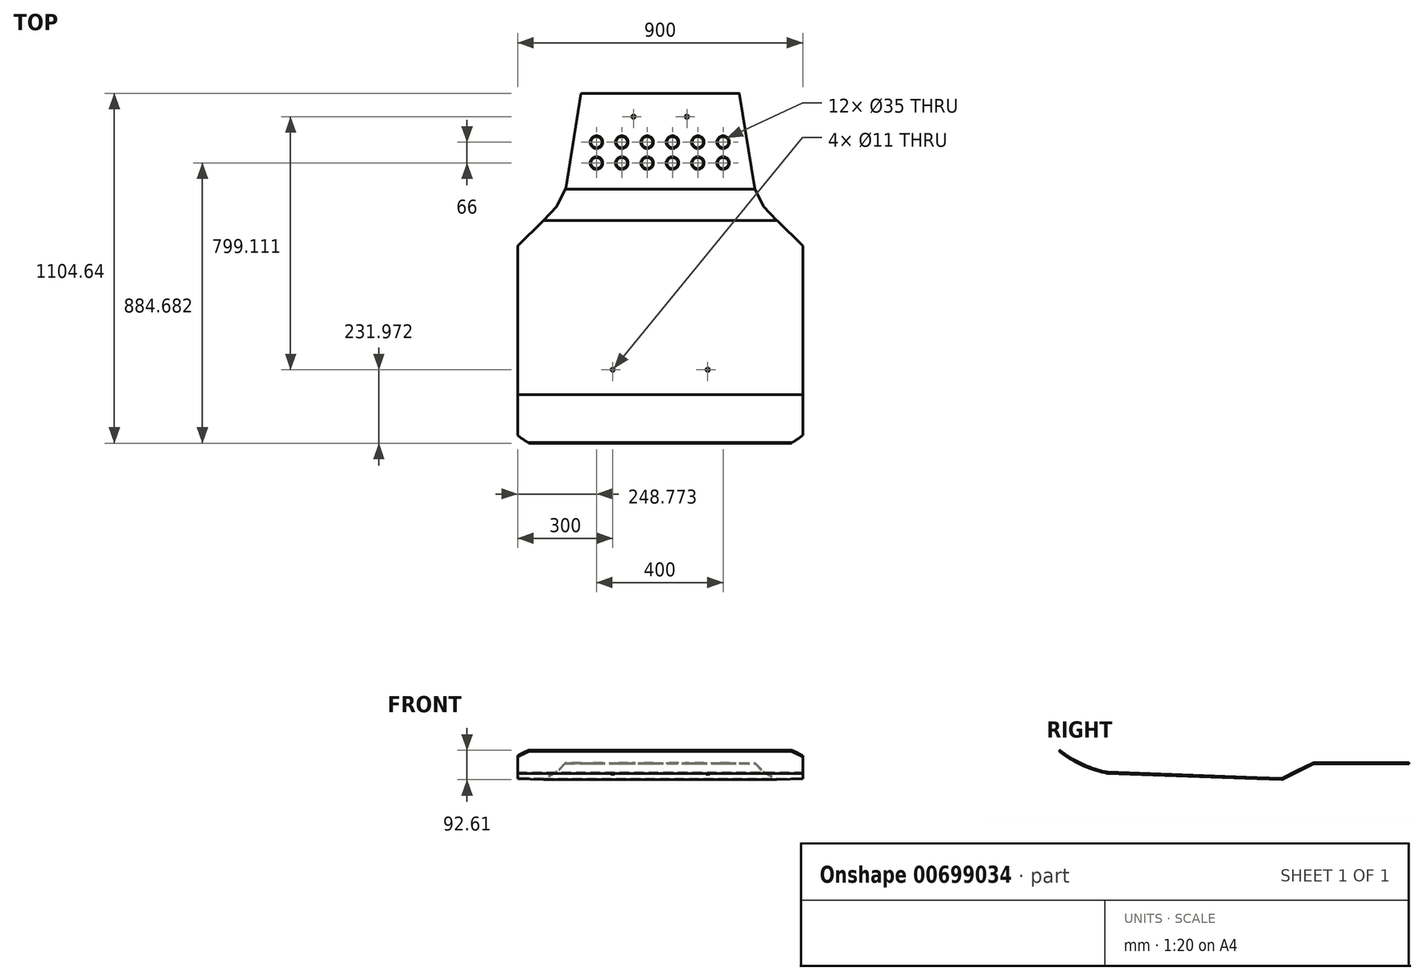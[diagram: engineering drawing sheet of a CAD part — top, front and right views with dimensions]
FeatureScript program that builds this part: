
annotation { "Feature Type Name" : "Feature", "Feature Type Description" : "" }
export const myFeature = defineFeature(function(context is Context, id is Id, definition is map)
    precondition{}
    {
        {
            var Q0;
            Q0=qCreatedBy(makeId("Right.planeOp"),FACE);
            cPlane(context, id + "F0", {"entities" : qUnion([Q0]), "cplaneType" : CPlaneType.OFFSET, "offset" : 450 * mm, "width" : 150 * mm, "height" : 150 * mm});
        }
        {
            var Q0;
            Q0=qCreatedBy(id+"F0.planeOp",FACE);
            var sketch = newSketch(context, id + "F1", { "sketchPlane" : qUnion([Q0])});
            skLineSegment(sketch, "E0", {"start": v(633.45, 19.14) * mm, "end": v(333.45, 19.14) * mm});
            skLineSegment(sketch, "E1", {"start": v(333.45, 19.14) * mm, "end": v(233.45, -30.86) * mm});
            skLineSegment(sketch, "E2", {"start": v(233.45, -30.86) * mm, "end": v(-316.55, -10.86) * mm});
            skArc(sketch, "E3", {"start": v(-316.55, -10.86) * mm, "mid": v(-395.73, 14.26) * mm, "end": v(-466.55, 57.68) * mm});
            skArc(sketch, "E4.0", {"start": v(-316.99, -14.85) * mm, "mid": v(-397.25, 10.56) * mm, "end": v(-469.03, 54.55) * mm});
            skLineSegment(sketch, "E4.1", {"start": v(234.33, -34.9) * mm, "end": v(-316.99, -14.85) * mm});
            skLineSegment(sketch, "E4.2", {"start": v(334.4, 15.14) * mm, "end": v(234.33, -34.9) * mm});
            skLineSegment(sketch, "E4.3", {"start": v(633.45, 15.14) * mm, "end": v(334.4, 15.14) * mm});
            skArc(sketch, "E5", {"start": v(-466.55, 57.68) * mm, "mid": v(-468.7, 56.83) * mm, "end": v(-469.03, 54.55) * mm});
            skArc(sketch, "E6", {"start": v(633.45, 15.14) * mm, "mid": v(635.45, 17.14) * mm, "end": v(633.45, 19.14) * mm});
            skSolve(sketch);
        }
        {
            var Q0;
            Q0=makeQuery(id+"F1.imprint","IMPRINT",FACE,{"disambiguationData":[TD([[makeQuery(id+"F1.imprint","IMPRINT",EDGE,{"derivedFrom":sQuery(id+"F1.wireOp",EDGE,"E0")}),1.0]])]});
            var Q1;
            Q1=qCreatedBy(makeId("Right.planeOp"),FACE);
            extrude(context, id + "F2", {"entities" : qUnion([Q0]), "endBound" : BoundingType.UP_TO_SURFACE, "oppositeDirection" : true, "depth" : 25 * mm, "endBoundEntityFace" : qUnion([Q1]), "offsetDistance" : 25 * mm});
        }
        {
            var Q0;
            Q0=qCreatedBy(makeId("Top.planeOp"),FACE);
            cPlane(context, id + "F3", {"entities" : qUnion([Q0]), "cplaneType" : CPlaneType.OFFSET, "offset" : 100 * mm, "width" : 150 * mm, "height" : 150 * mm});
        }
        {
            var Q0;
            Q0=qCreatedBy(id+"F3.planeOp",FACE);
            var sketch = newSketch(context, id + "F4", { "sketchPlane" : qUnion([Q0])});
            skLineSegment(sketch, "E7", {"start": v(218.78, 735.39) * mm, "end": v(237, 712.97) * mm});
            skLineSegment(sketch, "E8", {"start": v(237, 712.97) * mm, "end": v(297.96, 337.61) * mm});
            skLineSegment(sketch, "E9", {"start": v(326.32, 278.4) * mm, "end": v(368.65, 233.6) * mm});
            skLineSegment(sketch, "E10", {"start": v(368.65, 233.6) * mm, "end": v(451.1, 153.37) * mm});
            skLineSegment(sketch, "E11", {"start": v(451.1, 153.37) * mm, "end": v(483.61, 153.37) * mm});
            skLineSegment(sketch, "E12", {"start": v(483.61, 153.37) * mm, "end": v(498.52, 703.49) * mm});
            skLineSegment(sketch, "E13", {"start": v(498.52, 703.49) * mm, "end": v(218.78, 735.39) * mm});
            skLineSegment(sketch, "E14", {"start": v(297.96, 337.61) * mm, "end": v(326.32, 278.4) * mm});
            skSolve(sketch);
        }
        {
            var Q0;
            Q0=makeQuery(id+"F4.imprint","IMPRINT",FACE,{"disambiguationData":[TD([[makeQuery(id+"F4.imprint","IMPRINT",EDGE,{"derivedFrom":sQuery(id+"F4.wireOp",EDGE,"E7")}),1.0]])]});
            extrude(context, id + "F5", {"entities" : qUnion([Q0]), "operationType" : NewBodyOperationType.REMOVE, "oppositeDirection" : true, "depth" : 137 * mm, "offsetDistance" : 25 * mm});
        }
        {
            var Q0;
            Q0=qCreatedBy(id+"F3.planeOp",FACE);
            var sketch = newSketch(context, id + "F6", { "sketchPlane" : qUnion([Q0])});
            skArc(sketch, "E15", {"start": v(367.93, -489.56) * mm, "mid": v(427.88, -460.38) * mm, "end": v(478.84, -417.38) * mm});
            skLineSegment(sketch, "E16", {"start": v(478.84, -417.38) * mm, "end": v(478.84, -496.6) * mm});
            skLineSegment(sketch, "E17", {"start": v(478.84, -496.6) * mm, "end": v(367.93, -489.56) * mm});
            skSolve(sketch);
        }
        {
            var Q0;
            Q0=makeQuery(id+"F6.imprint","IMPRINT",FACE,{"disambiguationData":[TD([[makeQuery(id+"F6.imprint","IMPRINT",EDGE,{"derivedFrom":sQuery(id+"F6.wireOp",EDGE,"E15")}),-1.0]])]});
            extrude(context, id + "F7", {"entities" : qUnion([Q0]), "operationType" : NewBodyOperationType.REMOVE, "endBound" : BoundingType.THROUGH_ALL, "oppositeDirection" : true, "depth" : 100 * mm, "offsetDistance" : 25 * mm});
        }
        {
            var Q0;
            Q0=makeQuery(id+"F2.opExtrude","SWEPT_FACE",FACE,{"disambiguationData":[OSD([sQuery(id+"F1.wireOp",EDGE,"E0")])]});
            var sketch = newSketch(context, id + "F8", { "sketchPlane" : qUnion([Q0])});
            skCircle(sketch, "E18", {"center": v(84.24, 561.9) * mm, "radius": 13.36 * mm});
            skSolve(sketch);
        }
        {
            var Q0;
            Q0=sQuery(id+"F8.wireOp",VERTEX,"E18.center");
            var Q1;
            Q1=makeQuery(id+"F2.opExtrude","SWEPT_BODY",BODY,{"disambiguationData":[OSD([sQuery(id+"F1.wireOp",EDGE,"E0"),sQuery(id+"F1.wireOp",EDGE,"E1"),sQuery(id+"F1.wireOp",EDGE,"E2"),sQuery(id+"F1.wireOp",EDGE,"E3"),sQuery(id+"F1.wireOp",EDGE,"E4.0"),sQuery(id+"F1.wireOp",EDGE,"E4.1"),sQuery(id+"F1.wireOp",EDGE,"E4.2"),sQuery(id+"F1.wireOp",EDGE,"E4.3"),sQuery(id+"F1.wireOp",EDGE,"E5"),sQuery(id+"F1.wireOp",EDGE,"E6")])]});
            hole(context, id + "F9", {"style" : HoleStyle.SIMPLE, "endStyle" : HoleEndStyle.THROUGH, "standardTappedOrClearance" : lookupTablePath({ "standard" : "ISO", "fit" : "Normal", "size" : "M10", "type" : "Clearance" }), "standardBlindInLast" : lookupTablePath({ "fit" : "Standard", "standard" : "ISO", "size" : "M10", "type" : "Clearance" }), "holeDiameter" : 11 * mm, "majorDiameter" : 5 * mm, "isTappedThrough" : true, "tappedDepth" : 12 * mm, "tapClearance" : 3, "startFromSketch" : true, "locations" : qUnion([Q0]), "scope" : qUnion([Q1])});
        }
        {
            var Q0;
            Q0=makeQuery(id+"F2.opExtrude","SWEPT_BODY",BODY,{"disambiguationData":[OSD([sQuery(id+"F1.wireOp",EDGE,"E0"),sQuery(id+"F1.wireOp",EDGE,"E1"),sQuery(id+"F1.wireOp",EDGE,"E2"),sQuery(id+"F1.wireOp",EDGE,"E3"),sQuery(id+"F1.wireOp",EDGE,"E4.0"),sQuery(id+"F1.wireOp",EDGE,"E4.1"),sQuery(id+"F1.wireOp",EDGE,"E4.2"),sQuery(id+"F1.wireOp",EDGE,"E4.3"),sQuery(id+"F1.wireOp",EDGE,"E5"),sQuery(id+"F1.wireOp",EDGE,"E6")])]});
            var Q1;
            Q1=qCreatedBy(makeId("Right.planeOp"),FACE);
            mirror(context, id + "F10", {"operationType" : NewBodyOperationType.ADD, "entities" : qUnion([Q0]), "mirrorPlane" : qUnion([Q1])});
        }
        {
            var Q0;
            {var subQ0=makeQuery(id+"F2.opExtrude","SWEPT_FACE",FACE,{"disambiguationData":[OSD([sQuery(id+"F1.wireOp",EDGE,"E2")])]});Q0=makeQuery(id+"F10.boolean.opBoolean","MERGE",FACE,{"derivedFrom":[subQ0,makeQuery(id+"F10.opPattern","COPY",FACE,{"derivedFrom":subQ0,"instanceName":"1"})]});}
            var sketch = newSketch(context, id + "F11", { "sketchPlane" : qUnion([Q0])});
            skCircle(sketch, "E19", {"center": v(150, -236.43) * mm, "radius": 5 * mm});
            skCircle(sketch, "E20", {"center": v(-150, -236.43) * mm, "radius": 5 * mm});
            skSolve(sketch);
        }
        {
            var Q0;
            Q0=sQuery(id+"F11.wireOp",VERTEX,"E20.center");
            var Q1;
            Q1=sQuery(id+"F11.wireOp",VERTEX,"E19.center");
            var Q2;
            Q2=makeQuery(id+"F2.opExtrude","SWEPT_BODY",BODY,{"disambiguationData":[OSD([sQuery(id+"F1.wireOp",EDGE,"E0"),sQuery(id+"F1.wireOp",EDGE,"E1"),sQuery(id+"F1.wireOp",EDGE,"E2"),sQuery(id+"F1.wireOp",EDGE,"E3"),sQuery(id+"F1.wireOp",EDGE,"E4.0"),sQuery(id+"F1.wireOp",EDGE,"E4.1"),sQuery(id+"F1.wireOp",EDGE,"E4.2"),sQuery(id+"F1.wireOp",EDGE,"E4.3"),sQuery(id+"F1.wireOp",EDGE,"E5"),sQuery(id+"F1.wireOp",EDGE,"E6")])]});
            hole(context, id + "F12", {"style" : HoleStyle.SIMPLE, "endStyle" : HoleEndStyle.THROUGH, "standardTappedOrClearance" : lookupTablePath({ "standard" : "ISO", "fit" : "Normal", "size" : "M10", "type" : "Clearance" }), "standardBlindInLast" : lookupTablePath({ "fit" : "Standard", "standard" : "ISO", "size" : "M10", "type" : "Clearance" }), "holeDiameter" : 11 * mm, "majorDiameter" : 5 * mm, "isTappedThrough" : true, "tappedDepth" : 12 * mm, "tapClearance" : 3, "startFromSketch" : true, "locations" : qUnion([Q0, Q1]), "scope" : qUnion([Q2])});
        }
        {
            var Q0;
            {var subQ0=makeQuery(id+"F2.opExtrude","SWEPT_FACE",FACE,{"disambiguationData":[OSD([sQuery(id+"F1.wireOp",EDGE,"E0")])]});Q0=makeQuery(id+"F10.boolean.opBoolean","MERGE",FACE,{"derivedFrom":[subQ0,makeQuery(id+"F10.opPattern","COPY",FACE,{"derivedFrom":subQ0,"instanceName":"1"})]});}
            var sketch = newSketch(context, id + "F13", { "sketchPlane" : qUnion([Q0])});
            skCircle(sketch, "E21", {"center": v(198.77, 481.5) * mm, "radius": 20 * mm});
            skCircle(sketch, "E22.0.1.0", {"center": v(198.77, 415.5) * mm, "radius": 20 * mm});
            skCircle(sketch, "E22.1.0.0", {"center": v(118.77, 481.5) * mm, "radius": 20 * mm});
            skCircle(sketch, "E22.1.1.0", {"center": v(118.77, 415.5) * mm, "radius": 20 * mm});
            skCircle(sketch, "E22.2.0.0", {"center": v(38.77, 481.5) * mm, "radius": 20 * mm});
            skCircle(sketch, "E22.2.1.0", {"center": v(38.77, 415.5) * mm, "radius": 20 * mm});
            skCircle(sketch, "E22.3.0.0", {"center": v(-41.23, 481.5) * mm, "radius": 20 * mm});
            skCircle(sketch, "E22.3.1.0", {"center": v(-41.23, 415.5) * mm, "radius": 20 * mm});
            skCircle(sketch, "E22.4.0.0", {"center": v(-121.23, 481.5) * mm, "radius": 20 * mm});
            skCircle(sketch, "E22.4.1.0", {"center": v(-121.23, 415.5) * mm, "radius": 20 * mm});
            skCircle(sketch, "E22.5.0.0", {"center": v(-201.23, 481.5) * mm, "radius": 20 * mm});
            skCircle(sketch, "E22.5.1.0", {"center": v(-201.23, 415.5) * mm, "radius": 20 * mm});
            skLineSegment(sketch, "E22.direction1", {"start": v(198.77, 481.5) * mm, "end": v(118.77, 481.5) * mm, "construction": true});
            skLineSegment(sketch, "E22.direction2", {"start": v(198.77, 481.5) * mm, "end": v(198.77, 415.5) * mm, "construction": true});
            skSolve(sketch);
        }
        {
            var Q0;
            Q0=sQuery(id+"F13.wireOp",VERTEX,"E21.center");
            var Q1;
            Q1=sQuery(id+"F13.wireOp",VERTEX,"E22.1.0.0.center");
            var Q2;
            Q2=sQuery(id+"F13.wireOp",VERTEX,"E22.2.0.0.center");
            var Q3;
            Q3=sQuery(id+"F13.wireOp",VERTEX,"E22.3.0.0.center");
            var Q4;
            Q4=sQuery(id+"F13.wireOp",VERTEX,"E22.4.0.0.center");
            var Q5;
            Q5=sQuery(id+"F13.wireOp",VERTEX,"E22.5.0.0.center");
            var Q6;
            Q6=sQuery(id+"F13.wireOp",VERTEX,"E22.5.1.0.center");
            var Q7;
            Q7=sQuery(id+"F13.wireOp",VERTEX,"E22.4.1.0.center");
            var Q8;
            Q8=sQuery(id+"F13.wireOp",VERTEX,"E22.3.1.0.center");
            var Q9;
            Q9=sQuery(id+"F13.wireOp",VERTEX,"E22.2.1.0.center");
            var Q10;
            Q10=sQuery(id+"F13.wireOp",VERTEX,"E22.1.1.0.center");
            var Q11;
            Q11=sQuery(id+"F13.wireOp",VERTEX,"E22.0.1.0.center");
            var Q12;
            Q12=makeQuery(id+"F2.opExtrude","SWEPT_BODY",BODY,{"disambiguationData":[OSD([sQuery(id+"F1.wireOp",EDGE,"E0"),sQuery(id+"F1.wireOp",EDGE,"E1"),sQuery(id+"F1.wireOp",EDGE,"E2"),sQuery(id+"F1.wireOp",EDGE,"E3"),sQuery(id+"F1.wireOp",EDGE,"E4.0"),sQuery(id+"F1.wireOp",EDGE,"E4.1"),sQuery(id+"F1.wireOp",EDGE,"E4.2"),sQuery(id+"F1.wireOp",EDGE,"E4.3"),sQuery(id+"F1.wireOp",EDGE,"E5"),sQuery(id+"F1.wireOp",EDGE,"E6")])]});
            hole(context, id + "F14", {"style" : HoleStyle.C_SINK, "endStyle" : HoleEndStyle.THROUGH, "holeDiameter" : 35 * mm, "cSinkDiameter" : 40 * mm, "cSinkAngle" : 90 * degree, "majorDiameter" : 5 * mm, "isTappedThrough" : true, "tappedDepth" : 12 * mm, "tapClearance" : 3, "startFromSketch" : true, "locations" : qUnion([Q0, Q1, Q2, Q3, Q4, Q5, Q6, Q7, Q8, Q9, Q10, Q11]), "scope" : qUnion([Q12])});
        }
    });
